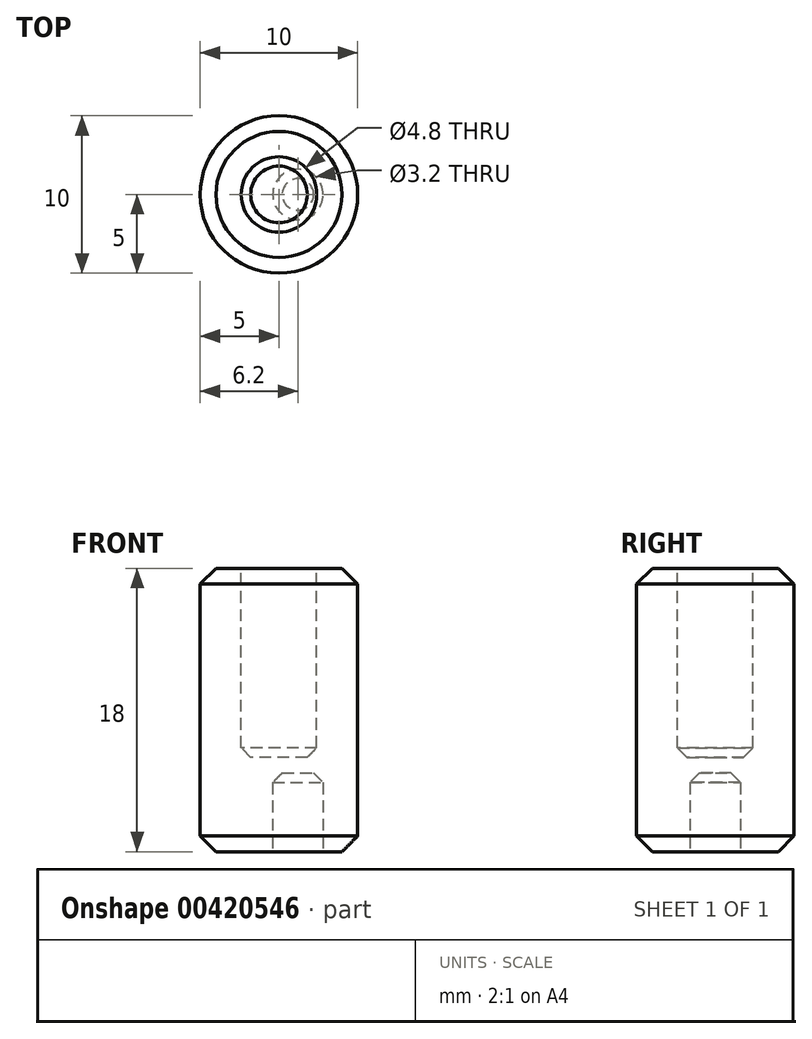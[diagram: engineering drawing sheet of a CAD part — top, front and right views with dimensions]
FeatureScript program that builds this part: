
annotation { "Feature Type Name" : "Feature", "Feature Type Description" : "" }
export const myFeature = defineFeature(function(context is Context, id is Id, definition is map)
    precondition{}
    {
        {
            var Q0;
            Q0=qCreatedBy(makeId("Top.planeOp"),FACE);
            var sketch = newSketch(context, id + "F0", { "sketchPlane" : qUnion([Q0])});
            skCircle(sketch, "E0", {"center": v(0, 0) * mm, "radius": 5 * mm});
            skSolve(sketch);
        }
        {
            var Q0;
            Q0=makeQuery(id+"F0.imprint","IMPRINT",FACE,{"disambiguationData":[TD([[makeQuery(id+"F0.imprint","IMPRINT",EDGE,{"derivedFrom":sQuery(id+"F0.wireOp",EDGE,"E0")}),1.0]])]});
            extrude(context, id + "F1", {"entities" : qUnion([Q0]), "depth" : 18 * mm});
        }
        {
            var Q0;
            Q0=makeQuery(id+"F1.opExtrude","CAP_FACE",FACE,{"disambiguationData":[OSD([sQuery(id+"F0.wireOp",EDGE,"E0")])],"isStart":false});
            var sketch = newSketch(context, id + "F2", { "sketchPlane" : qUnion([Q0])});
            skCircle(sketch, "E1", {"center": v(0, 0) * mm, "radius": 2.4 * mm});
            skSolve(sketch);
        }
        {
            var Q0;
            Q0=makeQuery(id+"F2.imprint","IMPRINT",FACE,{"disambiguationData":[TD([[makeQuery(id+"F2.imprint","IMPRINT",EDGE,{"derivedFrom":sQuery(id+"F2.wireOp",EDGE,"E1")}),1.0]])]});
            extrude(context, id + "F3", {"entities" : qUnion([Q0]), "operationType" : NewBodyOperationType.REMOVE, "oppositeDirection" : true, "depth" : 12 * mm});
        }
        {
            var Q0;
            Q0=makeQuery(id+"F1.opExtrude","CAP_FACE",FACE,{"disambiguationData":[OSD([sQuery(id+"F0.wireOp",EDGE,"E0")])],"isStart":true});
            var sketch = newSketch(context, id + "F4", { "sketchPlane" : qUnion([Q0])});
            skCircle(sketch, "E2", {"center": v(1.2, 0) * mm, "radius": 1.6 * mm});
            skSolve(sketch);
        }
        {
            var Q0;
            Q0=makeQuery(id+"F4.imprint","IMPRINT",FACE,{"disambiguationData":[TD([[makeQuery(id+"F4.imprint","IMPRINT",EDGE,{"derivedFrom":sQuery(id+"F4.wireOp",EDGE,"E2")}),1.0]])]});
            extrude(context, id + "F5", {"entities" : qUnion([Q0]), "operationType" : NewBodyOperationType.REMOVE, "oppositeDirection" : true, "depth" : 5 * mm});
        }
        {
            var Q0;
            Q0=makeQuery(id+"F5.boolean.opBoolean","COPY",FACE,{"derivedFrom":makeQuery(id+"F5.opExtrude","CAP_FACE",FACE,{"disambiguationData":[OSD([sQuery(id+"F4.wireOp",EDGE,"E2")])],"isStart":false})});
            var Q1;
            Q1=makeQuery(id+"F3.boolean.opBoolean","COPY",FACE,{"derivedFrom":makeQuery(id+"F3.opExtrude","CAP_FACE",FACE,{"disambiguationData":[OSD([sQuery(id+"F2.wireOp",EDGE,"E1")])],"isStart":false})});
            chamfer(context, id + "F6", {"entities" : qUnion([Q0, Q1]), "width" : .6 * mm, "tangentPropagation" : true});
        }
        {
            var Q0;
            Q0=makeQuery(id+"F1.opExtrude","CAP_EDGE",EDGE,{"disambiguationData":[OSD([sQuery(id+"F0.wireOp",EDGE,"E0")])],"isStart":true});
            var Q1;
            Q1=makeQuery(id+"F1.opExtrude","CAP_EDGE",EDGE,{"disambiguationData":[OSD([sQuery(id+"F0.wireOp",EDGE,"E0")])],"isStart":false});
            chamfer(context, id + "F7", {"entities" : qUnion([Q0, Q1]), "width" : 1 * mm, "tangentPropagation" : true});
        }
    });
